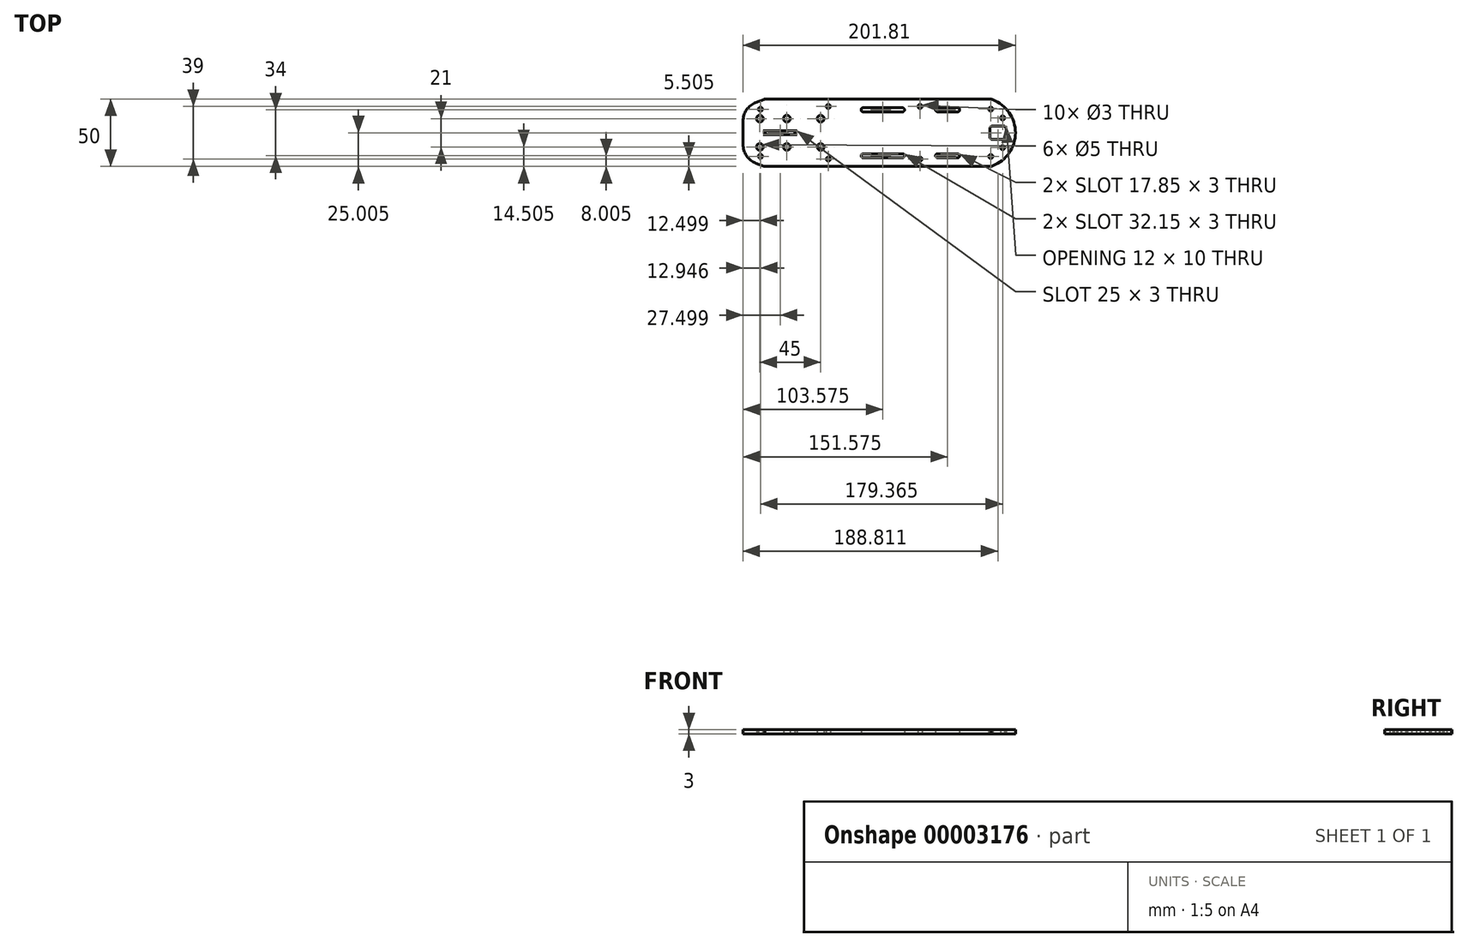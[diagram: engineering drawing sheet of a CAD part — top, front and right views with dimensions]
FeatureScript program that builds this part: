
annotation { "Feature Type Name" : "Feature", "Feature Type Description" : "" }
export const myFeature = defineFeature(function(context is Context, id is Id, definition is map)
    precondition{}
    {
        {
            var Q0;
            Q0=qCreatedBy(makeId("Top.planeOp"),FACE);
            var sketch = newSketch(context, id + "F0", { "sketchPlane" : qUnion([Q0])});
            skLineSegment(sketch, "E0", {"start": v(-72.92, 96.67) * mm, "end": v(-4.93, 96.67) * mm});
            skLineSegment(sketch, "E1", {"start": v(-4.93, 46.67) * mm, "end": v(-72.92, 46.67) * mm});
            skPoint(sketch, "E2.visualSharp", {"position": v(5.57, 96.67) * mm});
            skPoint(sketch, "E3.visualSharp", {"position": v(-84.43, 96.67) * mm});
            skPoint(sketch, "E4.visualSharp", {"position": v(-84.43, 46.67) * mm});
            skPoint(sketch, "E5.visualSharp", {"position": v(5.57, 46.67) * mm});
            skPoint(sketch, "E6.visualSharp", {"position": v(-112.13, 99.63) * mm});
            skPoint(sketch, "E7.visualSharp", {"position": v(-112.13, 43.72) * mm});
            skPoint(sketch, "E8", {"position": v(-123.13, 89.13) * mm});
            skCircle(sketch, "E9", {"center": v(-123.13, 89.13) * mm, "radius": 1.5 * mm});
            skPoint(sketch, "E10", {"position": v(-123.13, 54.22) * mm});
            skCircle(sketch, "E11", {"center": v(-123.13, 54.22) * mm, "radius": 1.5 * mm});
            skPoint(sketch, "E12", {"position": v(-72.92, 91.17) * mm});
            skCircle(sketch, "E13", {"center": v(-72.92, 91.17) * mm, "radius": 1.5 * mm});
            skPoint(sketch, "E14", {"position": v(-72.92, 52.17) * mm});
            skCircle(sketch, "E15", {"center": v(-72.92, 52.17) * mm, "radius": 1.5 * mm});
            skPoint(sketch, "E16", {"position": v(-4.93, 52.17) * mm});
            skCircle(sketch, "E17", {"center": v(-4.93, 52.17) * mm, "radius": 1.5 * mm});
            skPoint(sketch, "E18", {"position": v(-4.93, 91.17) * mm});
            skCircle(sketch, "E19", {"center": v(-4.93, 91.17) * mm, "radius": 1.5 * mm});
            skLineSegment(sketch, "E20", {"start": v(-136.08, 80.17) * mm, "end": v(-136.08, 63.17) * mm});
            skPoint(sketch, "E21", {"position": v(65.73, 71.67) * mm});
            skLineSegment(sketch, "E22", {"start": v(65.73, 71.67) * mm, "end": v(-136.08, 71.67) * mm});
            skPoint(sketch, "E23", {"position": v(-136.08, 89.67) * mm});
            skPoint(sketch, "E24", {"position": v(-136.08, 53.67) * mm});
            skLineSegment(sketch, "E25", {"start": v(-126.41, 94.2) * mm, "end": v(-120.58, 96.42) * mm});
            skLineSegment(sketch, "E26", {"start": v(-126.41, 49.15) * mm, "end": v(-120.58, 46.93) * mm});
            skArc(sketch, "E27.filletArc", {"start": v(-126.41, 94.2) * mm, "mid": v(-133.43, 88.69) * mm, "end": v(-136.08, 80.17) * mm});
            skArc(sketch, "E28.filletArc", {"start": v(-136.08, 63.17) * mm, "mid": v(-133.43, 54.66) * mm, "end": v(-126.41, 49.15) * mm});
            skArc(sketch, "E29.filletArc", {"start": v(-120.58, 96.42) * mm, "mid": v(-120.26, 96.54) * mm, "end": v(-119.96, 96.67) * mm});
            skArc(sketch, "E30", {"start": v(48.81, 47.15) * mm, "mid": v(65.73, 71.67) * mm, "end": v(48.81, 96.2) * mm});
            skPoint(sketch, "E31.visualSharp", {"position": v(33.43, 97.2) * mm});
            skPoint(sketch, "E32.visualSharp", {"position": v(33.43, 46.15) * mm});
            skArc(sketch, "E32.filletArc", {"start": v(48.81, 47.15) * mm, "mid": v(48.25, 46.92) * mm, "end": v(47.7, 46.67) * mm});
            skPoint(sketch, "E33", {"position": v(-71.08, 71.67) * mm});
            skPoint(sketch, "E34", {"position": v(-67.08, 71.67) * mm});
            skPoint(sketch, "E35", {"position": v(42.92, 71.67) * mm});
            skPoint(sketch, "E36", {"position": v(46.73, 71.67) * mm});
            skPoint(sketch, "E37", {"position": v(-71.08, 89.67) * mm});
            skPoint(sketch, "E38", {"position": v(-71.08, 53.67) * mm});
            skLineSegment(sketch, "E39.bottom", {"start": v(-71.08, 53.67) * mm, "end": v(-131.08, 53.67) * mm});
            skLineSegment(sketch, "E39.top", {"start": v(-71.08, 89.67) * mm, "end": v(-131.08, 89.67) * mm});
            skLineSegment(sketch, "E39.left", {"start": v(-71.08, 53.67) * mm, "end": v(-71.08, 89.67) * mm});
            skLineSegment(sketch, "E39.right", {"start": v(-131.08, 53.67) * mm, "end": v(-131.08, 89.67) * mm});
            skLineSegment(sketch, "E40.left", {"start": v(-67.08, 53.67) * mm, "end": v(-67.08, 89.67) * mm});
            skLineSegment(sketch, "E40.right", {"start": v(42.92, 53.67) * mm, "end": v(42.92, 89.67) * mm});
            skPoint(sketch, "E41", {"position": v(-67.08, 53.67) * mm});
            skLineSegment(sketch, "E42.bottom", {"start": v(48.73, 66.67) * mm, "end": v(56.73, 66.67) * mm});
            skLineSegment(sketch, "E42.top", {"start": v(48.73, 76.67) * mm, "end": v(56.73, 76.67) * mm});
            skLineSegment(sketch, "E42.left", {"start": v(46.73, 68.67) * mm, "end": v(46.73, 74.67) * mm});
            skLineSegment(sketch, "E42.right", {"start": v(58.73, 68.67) * mm, "end": v(58.73, 74.67) * mm});
            skPoint(sketch, "E43", {"position": v(46.73, 66.67) * mm});
            skPoint(sketch, "E44.visualSharp", {"position": v(58.73, 76.67) * mm});
            skArc(sketch, "E44.filletArc", {"start": v(58.73, 74.67) * mm, "mid": v(58.15, 76.09) * mm, "end": v(56.73, 76.67) * mm});
            skPoint(sketch, "E45.visualSharp", {"position": v(46.73, 76.67) * mm});
            skArc(sketch, "E45.filletArc", {"start": v(48.73, 76.67) * mm, "mid": v(47.32, 76.09) * mm, "end": v(46.73, 74.67) * mm});
            skArc(sketch, "E46.filletArc", {"start": v(46.73, 68.67) * mm, "mid": v(47.32, 67.26) * mm, "end": v(48.73, 66.67) * mm});
            skPoint(sketch, "E47.visualSharp", {"position": v(58.73, 66.67) * mm});
            skArc(sketch, "E47.filletArc", {"start": v(56.73, 66.67) * mm, "mid": v(58.15, 67.26) * mm, "end": v(58.73, 68.67) * mm});
            skPoint(sketch, "E48", {"position": v(47.43, 89.2) * mm});
            skPoint(sketch, "E49", {"position": v(47.43, 54.15) * mm});
            skCircle(sketch, "E50", {"center": v(47.43, 89.2) * mm, "radius": 1.5 * mm});
            skCircle(sketch, "E51", {"center": v(47.43, 54.15) * mm, "radius": 1.5 * mm});
            skLineSegment(sketch, "E52", {"start": v(-72.92, 46.67) * mm, "end": v(-119.96, 46.67) * mm});
            skArc(sketch, "E53", {"start": v(-119.96, 46.67) * mm, "mid": v(-120.26, 46.8) * mm, "end": v(-120.58, 46.93) * mm});
            skLineSegment(sketch, "E54", {"start": v(-72.92, 96.67) * mm, "end": v(-119.96, 96.67) * mm});
            skLineSegment(sketch, "E55", {"start": v(-4.93, 96.67) * mm, "end": v(47.63, 96.67) * mm});
            skArc(sketch, "E56", {"start": v(47.63, 96.67) * mm, "mid": v(48.21, 96.43) * mm, "end": v(48.81, 96.2) * mm});
            skLineSegment(sketch, "E57", {"start": v(-4.93, 46.67) * mm, "end": v(47.7, 46.67) * mm});
            skCircle(sketch, "E58", {"center": v(-78.58, 82.17) * mm, "radius": 2.5 * mm});
            skCircle(sketch, "E59", {"center": v(-78.58, 61.17) * mm, "radius": 2.5 * mm});
            skCircle(sketch, "E60", {"center": v(-123.58, 61.17) * mm, "radius": 2.5 * mm});
            skCircle(sketch, "E61", {"center": v(-123.58, 82.17) * mm, "radius": 2.5 * mm});
            skCircle(sketch, "E62", {"center": v(56.23, 82.67) * mm, "radius": 1.5 * mm});
            skCircle(sketch, "E63", {"center": v(56.23, 60.67) * mm, "radius": 1.5 * mm});
            skCircle(sketch, "E64", {"center": v(56.23, 82.67) * mm, "radius": 5.5 * mm});
            skCircle(sketch, "E65", {"center": v(56.23, 60.67) * mm, "radius": 5.5 * mm});
            skCircle(sketch, "E66", {"center": v(-103.58, 82.17) * mm, "radius": 2.5 * mm});
            skCircle(sketch, "E67", {"center": v(-103.58, 61.17) * mm, "radius": 2.5 * mm});
            skCircle(sketch, "E68", {"center": v(-121.08, 71.67) * mm, "radius": 1.5 * mm});
            skCircle(sketch, "E69", {"center": v(-96.08, 71.67) * mm, "radius": 1.5 * mm});
            skLineSegment(sketch, "E70", {"start": v(-92.29, 73.17) * mm, "end": v(-130.22, 73.17) * mm});
            skLineSegment(sketch, "E71", {"start": v(-130.05, 70.17) * mm, "end": v(-91.9, 70.17) * mm});
            skPoint(sketch, "E72", {"position": v(-47.08, 88.67) * mm});
            skPoint(sketch, "E73", {"position": v(-17.93, 88.67) * mm});
            skPoint(sketch, "E74", {"position": v(8.07, 88.67) * mm});
            skPoint(sketch, "E75", {"position": v(22.92, 88.67) * mm});
            skCircle(sketch, "E76", {"center": v(-47.08, 88.67) * mm, "radius": 1.5 * mm});
            skCircle(sketch, "E77", {"center": v(-17.93, 88.67) * mm, "radius": 1.5 * mm});
            skCircle(sketch, "E78", {"center": v(8.07, 88.67) * mm, "radius": 1.5 * mm});
            skCircle(sketch, "E79", {"center": v(22.92, 88.67) * mm, "radius": 1.5 * mm});
            skLineSegment(sketch, "E80", {"start": v(-14.23, 90.17) * mm, "end": v(-54.39, 90.17) * mm});
            skLineSegment(sketch, "E81", {"start": v(-52.06, 87.17) * mm, "end": v(-10.8, 87.17) * mm});
            skLineSegment(sketch, "E82", {"start": v(3.53, 90.17) * mm, "end": v(25.62, 90.17) * mm});
            skLineSegment(sketch, "E83", {"start": v(3.8, 87.17) * mm, "end": v(26.71, 87.17) * mm});
            skPoint(sketch, "E84", {"position": v(-47.08, 54.67) * mm});
            skPoint(sketch, "E85", {"position": v(-17.93, 54.67) * mm});
            skPoint(sketch, "E86", {"position": v(8.07, 54.67) * mm});
            skPoint(sketch, "E87", {"position": v(22.92, 54.67) * mm});
            skCircle(sketch, "E88", {"center": v(-47.08, 54.67) * mm, "radius": 1.5 * mm});
            skCircle(sketch, "E89", {"center": v(-17.93, 54.67) * mm, "radius": 1.5 * mm});
            skCircle(sketch, "E90", {"center": v(8.07, 54.67) * mm, "radius": 1.5 * mm});
            skCircle(sketch, "E91", {"center": v(22.92, 54.67) * mm, "radius": 1.5 * mm});
            skLineSegment(sketch, "E92", {"start": v(5, 56.17) * mm, "end": v(27.89, 56.17) * mm});
            skLineSegment(sketch, "E93", {"start": v(5.44, 53.17) * mm, "end": v(26.73, 53.17) * mm});
            skLineSegment(sketch, "E94", {"start": v(-49.75, 56.17) * mm, "end": v(-15, 56.17) * mm});
            skLineSegment(sketch, "E95", {"start": v(-48.69, 53.17) * mm, "end": v(-16.87, 53.17) * mm});
            skSolve(sketch);
        }
        {
            var Q0;
            {var subQ16=sQuery(id+"F0.wireOp",EDGE,"19b01eae-45ee-4ca3-8897-39b6d41e24321");Q0=makeQuery(id+"F0.imprint","IMPRINT",FACE,{"disambiguationData":[TD([[makeQuery(id+"F0.imprint","IMPRINT",EDGE,{"derivedFrom":subQ16}),1.0]])]});}
            var Q1;
            {var subQ20=sQuery(id+"F0.wireOp",EDGE,"8904a58b-4149-49d1-b910-17f218eac1cb");Q1=makeQuery(id+"F0.imprint","IMPRINT",FACE,{"disambiguationData":[TD([[makeQuery(id+"F0.imprint","IMPRINT",EDGE,{"derivedFrom":subQ20}),-1.0]])]});}
            var Q2;
            Q2=makeQuery(id+"F0.imprint","IMPRINT",FACE,{"disambiguationData":[TD([[makeQuery(id+"F0.imprint","IMPRINT",EDGE,{"derivedFrom":sQuery(id+"F0.wireOp",EDGE,"E0")}),-1.0]])]});
            var Q3;
            Q3=makeQuery(id+"F0.imprint","IMPRINT",FACE,{"disambiguationData":[TD([[makeQuery(id+"F0.imprint","IMPRINT",EDGE,{"derivedFrom":sQuery(id+"F0.wireOp",EDGE,"E9")}),-1.0]])]});
            var Q4;
            Q4=makeQuery(id+"F0.imprint","IMPRINT",FACE,{"disambiguationData":[TD([[makeQuery(id+"F0.imprint","IMPRINT",EDGE,{"derivedFrom":sQuery(id+"F0.wireOp",EDGE,"E11")}),-1.0]])]});
            var Q5;
            Q5=makeQuery(id+"F0.imprint","IMPRINT",FACE,{"disambiguationData":[TD([[makeQuery(id+"F0.imprint","IMPRINT",EDGE,{"derivedFrom":sQuery(id+"F0.wireOp",EDGE,"bf61aec3-fdc4-4691-a419-78ee3648398d")}),-1.0]])]});
            var Q6;
            {var subQ0=sQuery(id+"F0.wireOp",EDGE,"E40.right");var subQ1=sQuery(id+"F0.wireOp",EDGE,"E22");var subQ2=makeQuery(id+"F0.imprint","INTERSECT",VERTEX,{"derivedFrom":[subQ1,subQ0]});Q6=makeQuery(id+"F0.imprint","IMPRINT",FACE,{"disambiguationData":[TD([[makeQuery(id+"F0.imprint","IMPRINT",EDGE,{"disambiguationData":[TD([[subQ2,-1.0]])],"derivedFrom":subQ1}),1.0]])]});}
            var Q7;
            {var subQ0=sQuery(id+"F0.wireOp",EDGE,"E40.right");var subQ1=sQuery(id+"F0.wireOp",EDGE,"E22");var subQ2=makeQuery(id+"F0.imprint","INTERSECT",VERTEX,{"derivedFrom":[subQ1,subQ0]});Q7=makeQuery(id+"F0.imprint","IMPRINT",FACE,{"disambiguationData":[TD([[makeQuery(id+"F0.imprint","IMPRINT",EDGE,{"disambiguationData":[TD([[subQ2,-1.0]])],"derivedFrom":subQ1}),-1.0]])]});}
            var Q8;
            Q8=makeQuery(id+"F0.imprint","IMPRINT",FACE,{"disambiguationData":[TD([[makeQuery(id+"F0.imprint","IMPRINT",EDGE,{"derivedFrom":sQuery(id+"F0.wireOp",EDGE,"b977eb8a-e9e8-41df-97b8-f4c07ef17898")}),1.0]])]});
            var Q9;
            {var subQ16=sQuery(id+"F0.wireOp",EDGE,"07d321fd-fded-4ffe-844e-2f14b30021b71");Q9=makeQuery(id+"F0.imprint","IMPRINT",FACE,{"disambiguationData":[TD([[makeQuery(id+"F0.imprint","IMPRINT",EDGE,{"derivedFrom":subQ16}),1.0]])]});}
            var Q10;
            {var subQ16=sQuery(id+"F0.wireOp",EDGE,"17afc5a0-bc27-41c0-a643-31cc9f2e785c2");Q10=makeQuery(id+"F0.imprint","IMPRINT",FACE,{"disambiguationData":[TD([[makeQuery(id+"F0.imprint","IMPRINT",EDGE,{"derivedFrom":subQ16}),1.0]])]});}
            var Q11;
            {var subQ16=sQuery(id+"F0.wireOp",EDGE,"9e1d0cfa-3d80-47f7-bb17-0f86f19f9a851");Q11=makeQuery(id+"F0.imprint","IMPRINT",FACE,{"disambiguationData":[TD([[makeQuery(id+"F0.imprint","IMPRINT",EDGE,{"derivedFrom":subQ16}),1.0]])]});}
            var Q12;
            {var subQ0=sQuery(id+"F0.wireOp",EDGE,"01bf7b76-69dc-43dd-b464-7c1263d9a12e");var subQ3=sQuery(id+"F0.wireOp",EDGE,"b977eb8a-e9e8-41df-97b8-f4c07ef17898");var subQ4=makeQuery(id+"F0.imprint","INTERSECT",VERTEX,{"derivedFrom":[subQ3,subQ0]});Q12=makeQuery(id+"F0.imprint","IMPRINT",FACE,{"disambiguationData":[TD([[makeQuery(id+"F0.imprint","IMPRINT",EDGE,{"disambiguationData":[TD([[subQ4,-1.0]])],"derivedFrom":subQ3}),1.0]])]});}
            var Q13;
            Q13=makeQuery(id+"F0.imprint","IMPRINT",FACE,{"disambiguationData":[TD([[makeQuery(id+"F0.imprint","IMPRINT",EDGE,{"derivedFrom":sQuery(id+"F0.wireOp",EDGE,"E1")}),-1.0]])]});
            var Q14;
            Q14=makeQuery(id+"F0.imprint","IMPRINT",FACE,{"disambiguationData":[TD([[makeQuery(id+"F0.imprint","IMPRINT",EDGE,{"derivedFrom":sQuery(id+"F0.wireOp",EDGE,"E62")}),-1.0]])]});
            var Q15;
            Q15=makeQuery(id+"F0.imprint","IMPRINT",FACE,{"disambiguationData":[TD([[makeQuery(id+"F0.imprint","IMPRINT",EDGE,{"derivedFrom":sQuery(id+"F0.wireOp",EDGE,"E63")}),-1.0]])]});
            extrude(context, id + "F1", {"entities" : qUnion([Q0, Q1, Q2, Q3, Q4, Q5, Q6, Q7, Q8, Q9, Q10, Q11, Q12, Q13, Q14, Q15]), "depth" : 3 * mm});
        }
    });
